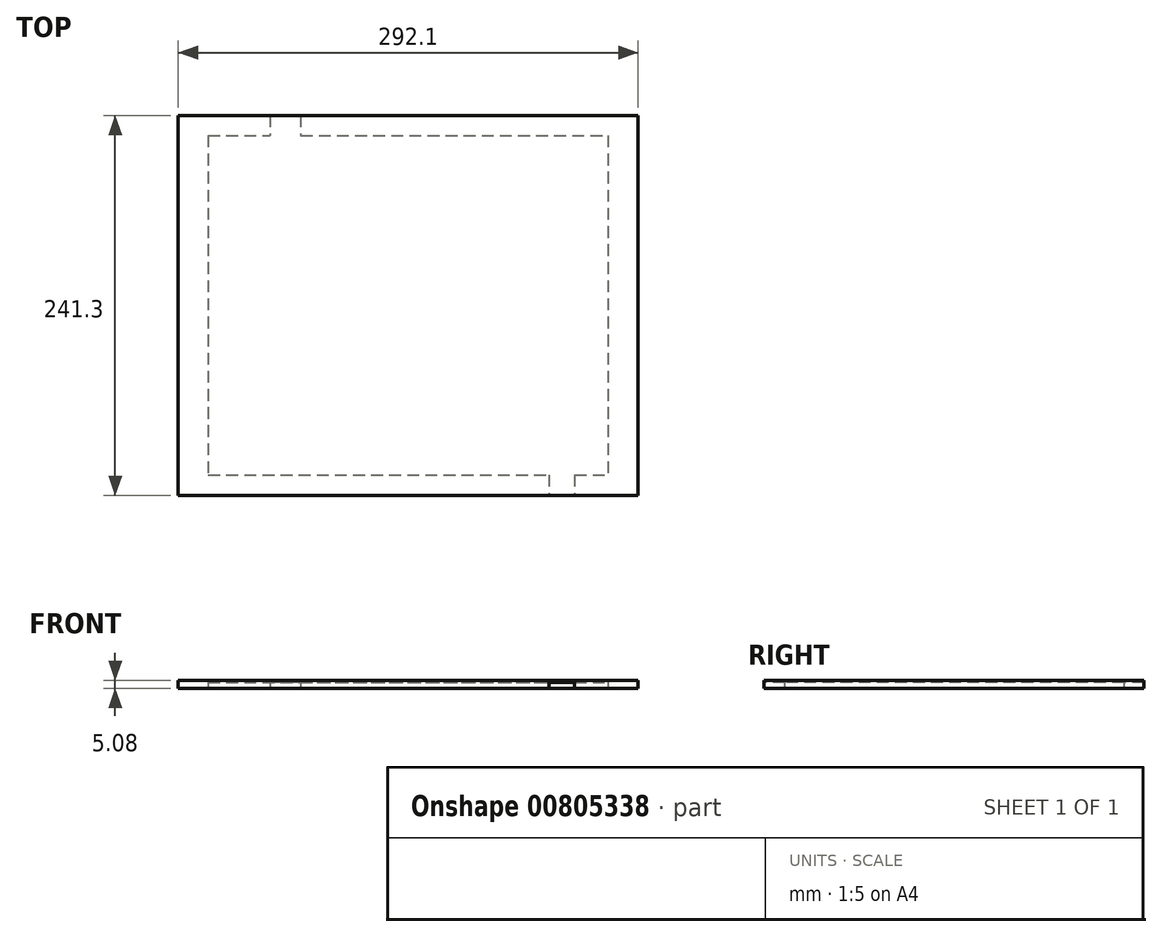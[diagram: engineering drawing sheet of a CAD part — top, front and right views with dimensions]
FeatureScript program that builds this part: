
annotation { "Feature Type Name" : "Feature", "Feature Type Description" : "" }
export const myFeature = defineFeature(function(context is Context, id is Id, definition is map)
    precondition{}
    {
        {
            var Q0;
            Q0=qCreatedBy(makeId("Top.planeOp"),FACE);
            var sketch = newSketch(context, id + "F0", { "sketchPlane" : qUnion([Q0])});
            skLineSegment(sketch, "E0.bottom", {"start": v(146.84, 120.36) * mm, "end": v(-145.26, 120.36) * mm});
            skLineSegment(sketch, "E0.top", {"start": v(146.84, -120.94) * mm, "end": v(-145.26, -120.94) * mm});
            skLineSegment(sketch, "E0.left", {"start": v(146.84, 120.36) * mm, "end": v(146.84, -120.94) * mm});
            skLineSegment(sketch, "E0.right", {"start": v(-145.26, 120.36) * mm, "end": v(-145.26, -120.94) * mm});
            skLineSegment(sketch, "E1.right", {"start": v(-126.2, -44.38) * mm, "end": v(-126.2, -107.88) * mm});
            skLineSegment(sketch, "E2.top", {"start": v(90.2, -122.1) * mm, "end": v(106.59, -122.1) * mm});
            skLineSegment(sketch, "E2.left", {"start": v(90.2, -107.83) * mm, "end": v(90.2, -122.1) * mm});
            skLineSegment(sketch, "E2.right", {"start": v(106.59, -107.83) * mm, "end": v(106.59, -122.1) * mm});
            skLineSegment(sketch, "E3.bottom", {"start": v(-126.2, 107.66) * mm, "end": v(127.8, 107.66) * mm});
            skLineSegment(sketch, "E3.top", {"start": v(-126.2, -107.88) * mm, "end": v(127.8, -107.88) * mm});
            skLineSegment(sketch, "E3.left", {"start": v(-126.2, 107.66) * mm, "end": v(-126.2, -107.88) * mm});
            skLineSegment(sketch, "E3.right", {"start": v(127.8, 107.66) * mm, "end": v(127.8, -107.88) * mm});
            skLineSegment(sketch, "E4.bottom", {"start": v(-86.94, 123.04) * mm, "end": v(-67.42, 123.04) * mm});
            skLineSegment(sketch, "E4.top", {"start": v(-86.94, 105.1) * mm, "end": v(-67.42, 105.1) * mm});
            skLineSegment(sketch, "E4.left", {"start": v(-86.94, 123.04) * mm, "end": v(-86.94, 105.1) * mm});
            skLineSegment(sketch, "E4.right", {"start": v(-67.42, 123.04) * mm, "end": v(-67.42, 105.1) * mm});
            skSolve(sketch);
        }
        {
            var Q0;
            {var subQ8=sQuery(id+"F0.wireOp",EDGE,"E0.right");Q0=makeQuery(id+"F0.imprint","IMPRINT",FACE,{"disambiguationData":[TD([[makeQuery(id+"F0.imprint","IMPRINT",EDGE,{"derivedFrom":subQ8}),1.0]])]});}
            var Q1;
            {var subQ5=sQuery(id+"F0.wireOp",EDGE,"E0.left");Q1=makeQuery(id+"F0.imprint","IMPRINT",FACE,{"disambiguationData":[TD([[makeQuery(id+"F0.imprint","IMPRINT",EDGE,{"derivedFrom":subQ5}),-1.0]])]});}
            var Q2;
            {var subQ0=sQuery(id+"F0.wireOp",EDGE,"E4.right");var subQ1=sQuery(id+"F0.wireOp",EDGE,"E0.bottom");var subQ2=makeQuery(id+"F0.imprint","INTERSECT",VERTEX,{"derivedFrom":[subQ1,subQ0]});Q2=makeQuery(id+"F0.imprint","IMPRINT",FACE,{"disambiguationData":[TD([[makeQuery(id+"F0.imprint","IMPRINT",EDGE,{"disambiguationData":[TD([[subQ2,-1.0]])],"derivedFrom":subQ1}),1.0]])]});}
            var Q3;
            {var subQ0=sQuery(id+"F0.wireOp",EDGE,"E2.right");var subQ1=sQuery(id+"F0.wireOp",EDGE,"E0.top");var subQ2=makeQuery(id+"F0.imprint","INTERSECT",VERTEX,{"derivedFrom":[subQ1,subQ0]});Q3=makeQuery(id+"F0.imprint","IMPRINT",FACE,{"disambiguationData":[TD([[makeQuery(id+"F0.imprint","IMPRINT",EDGE,{"disambiguationData":[TD([[subQ2,-1.0]])],"derivedFrom":subQ1}),-1.0]])]});}
            extrude(context, id + "F1", {"entities" : qUnion([Q0, Q1, Q2, Q3]), "depth" : 5.08 * mm, "offsetDistance" : 25.4 * mm});
        }
        {
            var Q0;
            {var subQ1=sQuery(id+"F0.wireOp",EDGE,"E3.right");Q0=makeQuery(id+"F0.imprint","IMPRINT",FACE,{"disambiguationData":[TD([[makeQuery(id+"F0.imprint","IMPRINT",EDGE,{"derivedFrom":subQ1}),-1.0]])]});}
            var Q1;
            {var subQ5=sQuery(id+"F0.wireOp",EDGE,"E4.top");Q1=makeQuery(id+"F0.imprint","IMPRINT",FACE,{"disambiguationData":[TD([[makeQuery(id+"F0.imprint","IMPRINT",EDGE,{"derivedFrom":subQ5}),1.0]])]});}
            extrude(context, id + "F2", {"entities" : qUnion([Q0, Q1]), "operationType" : NewBodyOperationType.ADD, "depth" : 5.08 * mm, "offsetDistance" : 25.4 * mm});
        }
        {
            var Q0;
            {var subQ1=sQuery(id+"F0.wireOp",EDGE,"E3.right");Q0=makeQuery(id+"F0.imprint","IMPRINT",FACE,{"disambiguationData":[TD([[makeQuery(id+"F0.imprint","IMPRINT",EDGE,{"derivedFrom":subQ1}),-1.0]])]});}
            var Q1;
            {var subQ5=sQuery(id+"F0.wireOp",EDGE,"E4.top");Q1=makeQuery(id+"F0.imprint","IMPRINT",FACE,{"disambiguationData":[TD([[makeQuery(id+"F0.imprint","IMPRINT",EDGE,{"derivedFrom":subQ5}),1.0]])]});}
            extrude(context, id + "F3", {"entities" : qUnion([Q0, Q1]), "operationType" : NewBodyOperationType.REMOVE, "oppositeDirection" : true, "depth" : -3.8 * mm, "offsetDistance" : 25.4 * mm});
        }
        {
            var Q0;
            {var subQ0=sQuery(id+"F0.wireOp",EDGE,"E2.right");var subQ1=sQuery(id+"F0.wireOp",EDGE,"E0.top");var subQ2=makeQuery(id+"F0.imprint","INTERSECT",VERTEX,{"derivedFrom":[subQ1,subQ0]});Q0=makeQuery(id+"F0.imprint","IMPRINT",FACE,{"disambiguationData":[TD([[makeQuery(id+"F0.imprint","IMPRINT",EDGE,{"disambiguationData":[TD([[subQ2,-1.0]])],"derivedFrom":subQ1}),-1.0]])]});}
            var Q1;
            {var subQ0=sQuery(id+"F0.wireOp",EDGE,"E4.right");var subQ1=sQuery(id+"F0.wireOp",EDGE,"E0.bottom");var subQ2=makeQuery(id+"F0.imprint","INTERSECT",VERTEX,{"derivedFrom":[subQ1,subQ0]});Q1=makeQuery(id+"F0.imprint","IMPRINT",FACE,{"disambiguationData":[TD([[makeQuery(id+"F0.imprint","IMPRINT",EDGE,{"disambiguationData":[TD([[subQ2,-1.0]])],"derivedFrom":subQ1}),1.0]])]});}
            extrude(context, id + "F4", {"entities" : qUnion([Q0, Q1]), "operationType" : NewBodyOperationType.REMOVE, "oppositeDirection" : true, "depth" : -3.8 * mm, "offsetDistance" : 25.4 * mm});
        }
    });
